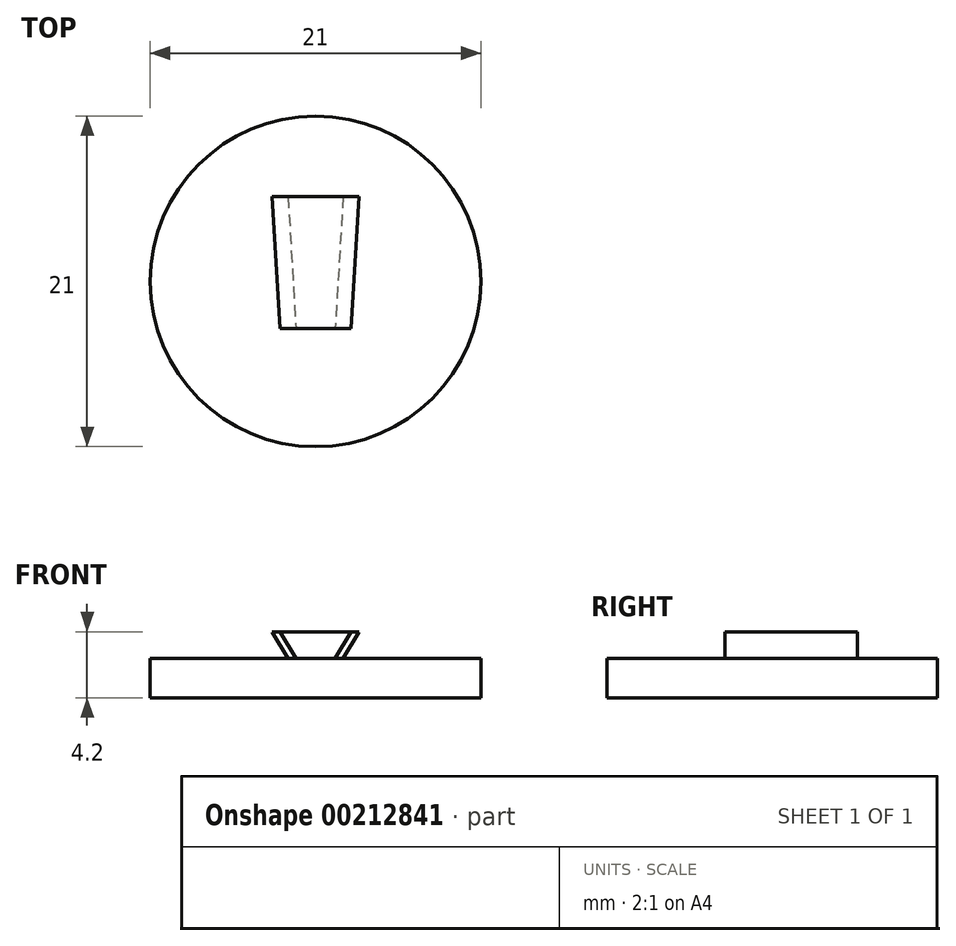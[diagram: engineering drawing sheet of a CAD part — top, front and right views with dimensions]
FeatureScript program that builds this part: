
annotation { "Feature Type Name" : "Feature", "Feature Type Description" : "" }
export const myFeature = defineFeature(function(context is Context, id is Id, definition is map)
    precondition{}
    {
        {
            var Q0;
            Q0=qCreatedBy(makeId("Top.planeOp"),FACE);
            var sketch = newSketch(context, id + "F0", { "sketchPlane" : qUnion([Q0])});
            skCircle(sketch, "E0", {"center": v(0, 0) * mm, "radius": 10.5 * mm});
            skSolve(sketch);
        }
        {
            var Q0;
            Q0 = qSketchRegion(id + "F0", true);
            extrude(context, id + "F1", {"entities" : qUnion([Q0]), "oppositeDirection" : true, "depth" : 2.5 * mm});
        }
        {
            var Q0;
            Q0=qCreatedBy(makeId("Front.planeOp"),FACE);
            cPlane(context, id + "F2", {"entities" : qUnion([Q0]), "cplaneType" : CPlaneType.OFFSET, "offset" : 3 * mm, "width" : 150 * mm, "height" : 150 * mm});
        }
        {
            var Q0;
            Q0=qCreatedBy(id+"F2.planeOp",FACE);
            var sketch = newSketch(context, id + "F3", { "sketchPlane" : qUnion([Q0])});
            skLineSegment(sketch, "E1", {"start": v(1.25, 0) * mm, "end": v(2.25, 1.7) * mm});
            skLineSegment(sketch, "E2", {"start": v(2.25, 1.7) * mm, "end": v(-2.25, 1.7) * mm});
            skLineSegment(sketch, "E3", {"start": v(-1.25, 0) * mm, "end": v(1.25, 0) * mm});
            skLineSegment(sketch, "E4.MirrorCS", {"start": v(-1.25, 0) * mm, "end": v(-2.25, 1.7) * mm});
            skSolve(sketch);
        }
        {
            var Q0;
            Q0=qCreatedBy(makeId("Front.planeOp"),FACE);
            cPlane(context, id + "F4", {"entities" : qUnion([Q0]), "cplaneType" : CPlaneType.OFFSET, "offset" : 5.4 * mm, "oppositeDirection" : true, "width" : 150 * mm, "height" : 150 * mm});
        }
        {
            var Q0;
            Q0=qCreatedBy(id+"F4.planeOp",FACE);
            var sketch = newSketch(context, id + "F5", { "sketchPlane" : qUnion([Q0])});
            skLineSegment(sketch, "E5", {"start": v(1.75, 0) * mm, "end": v(2.75, 1.7) * mm});
            skLineSegment(sketch, "E6", {"start": v(2.75, 1.7) * mm, "end": v(-2.75, 1.7) * mm});
            skLineSegment(sketch, "E7", {"start": v(-1.75, 0) * mm, "end": v(1.75, 0) * mm});
            skLineSegment(sketch, "E8.MirrorCS", {"start": v(-1.75, 0) * mm, "end": v(-2.75, 1.7) * mm});
            skSolve(sketch);
        }
        {
            var Q1;
            Q1 = qSketchRegion(id + "F5", true);
            var Q2;
            Q2 = qSketchRegion(id + "F3", true);
            loft(context, id + "F6", {"operationType" : NewBodyOperationType.ADD, "sheetProfilesArray" : [{ "sheetProfileEntities" : qUnion([Q1]) }, { "sheetProfileEntities" : qUnion([Q2]) }]});
        }
    });
